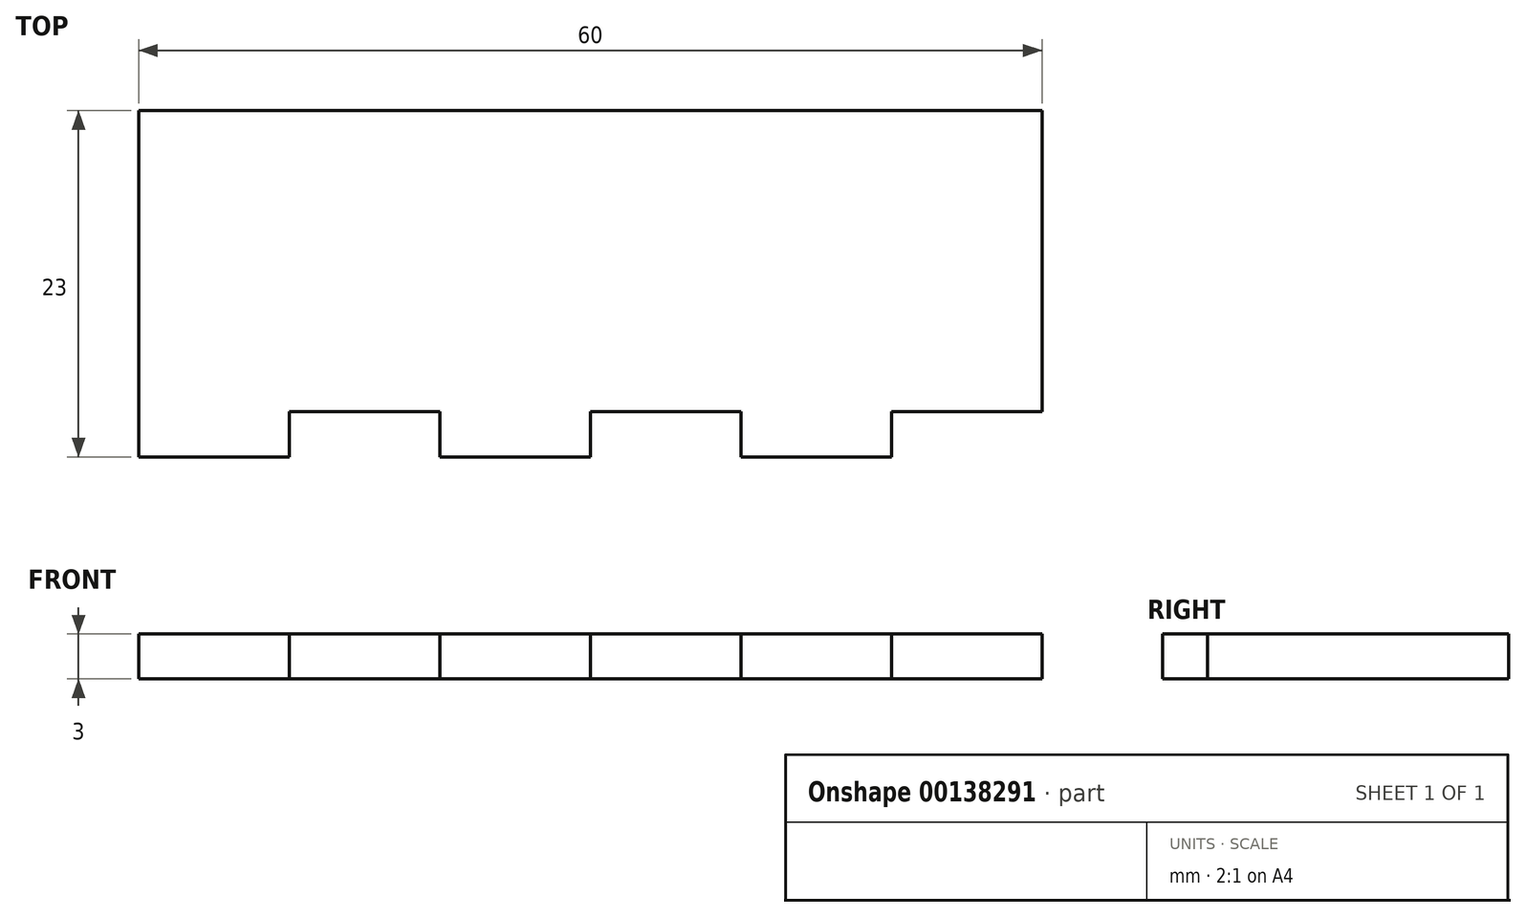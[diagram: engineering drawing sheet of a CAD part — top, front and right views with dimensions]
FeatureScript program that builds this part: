
annotation { "Feature Type Name" : "Feature", "Feature Type Description" : "" }
export const myFeature = defineFeature(function(context is Context, id is Id, definition is map)
    precondition{}
    {
        {
            var Q0;
            Q0=qCreatedBy(makeId("Top.planeOp"),FACE);
            var sketch = newSketch(context, id + "F0", { "sketchPlane" : qUnion([Q0])});
            skLineSegment(sketch, "E0.bottom", {"start": v(-30, 10) * mm, "end": v(30, 10) * mm});
            skLineSegment(sketch, "E0.top", {"start": v(-20, -10) * mm, "end": v(-10, -10) * mm});
            skLineSegment(sketch, "E0.left", {"start": v(-30, 10) * mm, "end": v(-30, -10) * mm});
            skLineSegment(sketch, "E0.right", {"start": v(30, 10) * mm, "end": v(30, -10) * mm});
            skPoint(sketch, "E0.middle", {"position": v(0, 0) * mm});
            skLineSegment(sketch, "E1", {"start": v(-20, -10) * mm, "end": v(-10, -10) * mm, "construction": true});
            skLineSegment(sketch, "E2", {"start": v(0, -10) * mm, "end": v(10, -10) * mm, "construction": true});
            skLineSegment(sketch, "E3", {"start": v(20, -10) * mm, "end": v(30, -10) * mm, "construction": true});
            skLineSegment(sketch, "E4.top", {"start": v(-30, -13) * mm, "end": v(-20, -13) * mm});
            skLineSegment(sketch, "E4.left", {"start": v(-30, -10) * mm, "end": v(-30, -13) * mm});
            skLineSegment(sketch, "E4.right", {"start": v(-20, -10) * mm, "end": v(-20, -13) * mm});
            skLineSegment(sketch, "E5.top", {"start": v(-10, -13) * mm, "end": v(0, -13) * mm});
            skLineSegment(sketch, "E5.left", {"start": v(-10, -10) * mm, "end": v(-10, -13) * mm});
            skLineSegment(sketch, "E5.right", {"start": v(0, -10) * mm, "end": v(0, -13) * mm});
            skLineSegment(sketch, "E6.top", {"start": v(10, -13) * mm, "end": v(20, -13) * mm});
            skLineSegment(sketch, "E6.left", {"start": v(10, -10) * mm, "end": v(10, -13) * mm});
            skLineSegment(sketch, "E6.right", {"start": v(20, -10) * mm, "end": v(20, -13) * mm});
            skLineSegment(sketch, "E7.trimOffspring", {"start": v(20, -10) * mm, "end": v(30, -10) * mm});
            skLineSegment(sketch, "E8.trimOffspring", {"start": v(0, -10) * mm, "end": v(10, -10) * mm});
            skSolve(sketch);
        }
        {
            var Q0;
            Q0=makeQuery(id+"F0.imprint","IMPRINT",FACE,{"disambiguationData":[TD([[makeQuery(id+"F0.imprint","IMPRINT",EDGE,{"derivedFrom":sQuery(id+"F0.wireOp",EDGE,"E0.bottom")}),-1.0]])]});
            extrude(context, id + "F1", {"entities" : qUnion([Q0]), "endBound" : BoundingType.SYMMETRIC, "depth" : 3 * mm});
        }
    });
